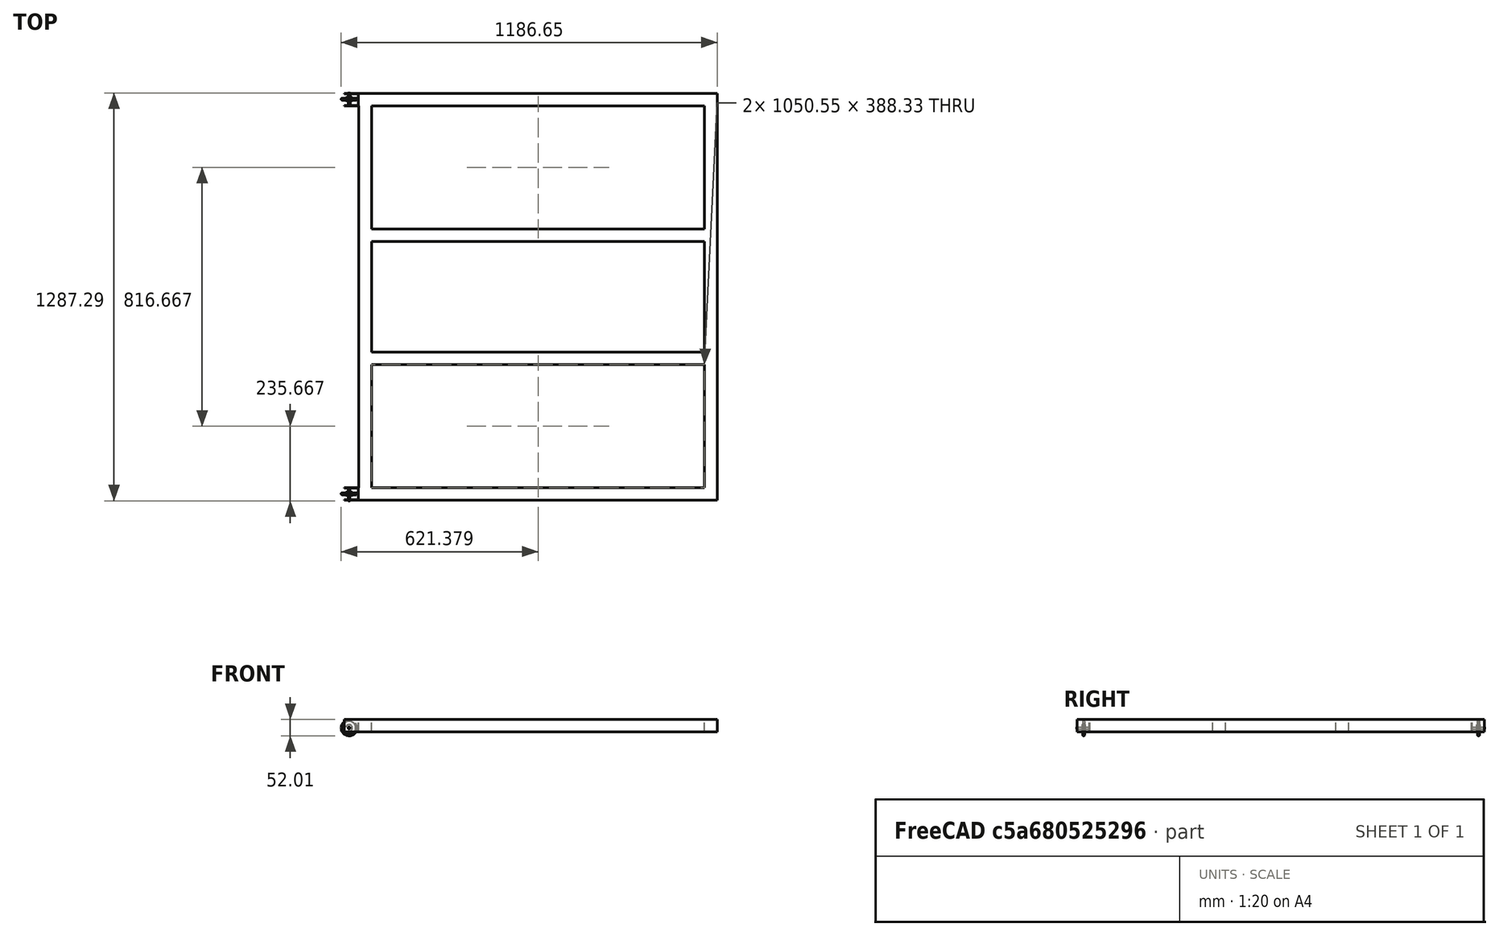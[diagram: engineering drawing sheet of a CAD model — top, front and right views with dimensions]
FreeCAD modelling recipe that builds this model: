
FCSTD DOCUMENT  (FreeCAD 0.19R24267 +148 (Git))
Label: planche jacuzzyV2
License: All rights reserved
LicenseURL: http://en.wikipedia.org/wiki/All_rights_reserved
objects: TechDraw::DrawViewDimension×9, PartDesign::Body×3, TechDraw::DrawViewPart×3, Sketcher::SketchObject×2, TechDraw::DrawViewDetail×2, PartDesign::Pad×1, PartDesign::Mirrored×1, TechDraw::DrawSVGTemplate×1, TechDraw::DrawProjGroupItem×1, TechDraw::DrawProjGroup×1, PartDesign::Revolution×1, PartDesign::FeatureBase×1, TechDraw::DrawViewSymbol×1, TechDraw::DrawPage×1
note: 11 computed .brp shape members not serialized (recipe doc carries the construction recipe); baked Part::Feature solids carry a one-line shape summary decoded from their .brp

FEATURE [Sketcher::SketchObject] Sketch
  FullyConstrained = false
  MapMode = 5
  Support = -> [XY_Plane]
  sketch-geometry (20):
    g0: LineSegment StartX=-403.347 StartY=642.5 StartZ=0 EndX=773.653 EndY=642.5 EndZ=0
    g1: LineSegment StartX=773.653 StartY=642.5 StartZ=0 EndX=733.653 EndY=602.5 EndZ=0
    g2: LineSegment StartX=733.653 StartY=602.5 StartZ=0 EndX=-316.896 EndY=602.5 EndZ=0
    g3: LineSegment StartX=-403.347 StartY=602.5 StartZ=0 EndX=-403.347 EndY=604 EndZ=0
    g4: LineSegment StartX=733.653 StartY=602.5 StartZ=0 EndX=773.653 EndY=642.5 EndZ=0
    g5: LineSegment StartX=773.653 StartY=642.5 StartZ=0 EndX=773.653 EndY=0 EndZ=0
    g6: LineSegment StartX=773.653 StartY=0 StartZ=0 EndX=733.653 EndY=0 EndZ=0
    g7: LineSegment StartX=733.653 StartY=0 StartZ=0 EndX=733.653 EndY=174.167 EndZ=0
    g8: LineSegment StartX=-316.896 StartY=602.5 StartZ=0 EndX=-316.896 EndY=214.167 EndZ=0
    g9: LineSegment StartX=-316.896 StartY=0 StartZ=0 EndX=-356.896 EndY=0 EndZ=0
    g10: LineSegment StartX=-356.896 StartY=0 StartZ=0 EndX=-356.896 EndY=602.5 EndZ=0
    g11: LineSegment StartX=-356.896 StartY=602.5 StartZ=0 EndX=-403.347 EndY=602.5 EndZ=0
    g12: LineSegment StartX=-316.896 StartY=214.167 StartZ=0 EndX=733.653 EndY=214.167 EndZ=0
    g13: LineSegment StartX=733.653 StartY=174.167 StartZ=0 EndX=-316.896 EndY=174.167 EndZ=0
    g14: LineSegment StartX=733.653 StartY=214.167 StartZ=0 EndX=733.653 EndY=602.5 EndZ=0
    g15: LineSegment StartX=-316.896 StartY=174.167 StartZ=0 EndX=-316.896 EndY=0 EndZ=0
    g16: LineSegment StartX=-403.347 StartY=641 StartZ=0 EndX=-358.347 EndY=641 EndZ=0
    g17: LineSegment StartX=-358.347 StartY=641 StartZ=0 EndX=-358.347 EndY=604 EndZ=0
    g18: LineSegment StartX=-358.347 StartY=604 StartZ=0 EndX=-403.347 EndY=604 EndZ=0
    g19: LineSegment StartX=-403.347 StartY=641 StartZ=0 EndX=-403.347 EndY=642.5 EndZ=0
  constraints (52):
    c: Coincident(g0,g1)
    c: Coincident(g1,g2)
    c: Coincident(g11,g3)
    c: Coincident(g19,g0)
    c: Horizontal(g0)
    c: Horizontal(g2)
    c: Vertical(g3)
    c: DistanceY(g3,g19) = 40
    c: DistanceX(g0,g0) = 1177
    c: Angle(g0,g1) = 0.785398
    c: DistanceY(g-1,g0) = 642.5
    c: Coincident(g4,g5)
    c: Coincident(g5,g6)
    c: Coincident(g6,g7)
    c: Coincident(g14,g4)
    c: Horizontal(g6)
    c: Vertical(g5)
    c: Vertical(g7)
    c: PointOnObject(g5,g-1)
    c: Coincident(g4,g1)
    c: Coincident(g0,g4)
    c: Coincident(g15,g9)
    c: Coincident(g9,g10)
    c: Horizontal(g9)
    c: Vertical(g8)
    c: Vertical(g10)
    c: PointOnObject(g15,g-1)
    c: DistanceX(g9,g9) = 40
    c: Tangent(g2,g11)
    c: Horizontal(g12)
    c: Horizontal(g13)
    c: DistanceY(g13,g12) = 40
    c: Tangent(g7,g14)
    c: Coincident(g8,g12)
    c: Tangent(g8,g15)
    c: DistanceY(g12,g1) = 388.333
    c: Coincident(g7,g13)
    c: Coincident(g13,g15)
    c: Coincident(g8,g2)
    c: Coincident(g11,g10)
    c: Coincident(g14,g12)
    c: Horizontal(g16)
    c: Coincident(g16,g17)
    c: Vertical(g17)
    c: Coincident(g17,g18)
    c: Horizontal(g18)
    c: DistanceY(g16,g0) = 1.5
    c: DistanceY(g3,g18) = 1.5
    c: DistanceX(g16,g16) = 45
    c: Coincident(g3,g18)
    c: Coincident(g19,g16)
    c: Tangent(g3,g19)
FEATURE [PartDesign::Pad] Pad
  Direction = (1,1,1)
  Length = 40
  Length2 = 100
  Profile = -> Sketch
  Type = 0
FEATURE [PartDesign::Mirrored] Mirrored
  BaseFeature = -> Pad
  MirrorPlane = -> XZ_Plane
  Originals = -> [Pad]
FEATURE [PartDesign::Body] Body
  Group = -> [Sketch,Pad,Mirrored]
  Origin = -> Origin
  Tip = -> Mirrored
FEATURE [TechDraw::DrawSVGTemplate] Template
  EditableTexts = Designed_by_Name=Labrit Yvan; Drawing_number=Drawing number; FC-Date=20/06/2022; FC-SC=Scale; FC-SH=Sheet; FC-Title=Trappe Jacuzzi; Subtitle=Subtitle; Weight=Weight
  Height = 210
  Orientation = 1
  Width = 297
FEATURE [TechDraw::DrawViewPart] View
  CoarseView = false
  Direction = (-0.472,0.816,0.334)
  Focus = 100
  HardHidden = false
  IsoCount = 0
  IsoHidden = false
  IsoVisible = false
  LockPosition = false
  Perspective = false
  Rotation = 0
  Scale = 0.08
  ScaleType = 0
  SeamHidden = false
  SeamVisible = true
  SmoothHidden = false
  SmoothVisible = true
  Source = -> [Mirrored]
  X = 208.733
  XDirection = (-0.861,-0.508,0.024)
  Y = 152.393
FEATURE [TechDraw::DrawProjGroupItem] ProjItem001  label="Front001"
  CoarseView = false
  Direction = (0,0,1)
  Focus = 100
  HardHidden = false
  IsoCount = 0
  IsoHidden = false
  IsoVisible = false
  LockPosition = true
  Perspective = false
  Rotation = 0
  RotationVector = (0,-1,0)
  Scale = 0.05
  ScaleType = 2
  SeamHidden = false
  SeamVisible = true
  SmoothHidden = false
  SmoothVisible = true
  Source = -> [Mirrored]
  Type = 0
  X = 0
  XDirection = (0,-1,0)
  Y = 0
FEATURE [TechDraw::DrawProjGroup] ProjGroup001
  Anchor = -> ProjItem001
  AutoDistribute = true
  LockPosition = false
  ProjectionType = 0
  Rotation = 0
  Scale = 0.05
  ScaleType = 0
  Source = -> [Mirrored]
  Views = -> [ProjItem001]
  X = 97.9019
  Y = 147.642
  spacingX = 15
  spacingY = 15
FEATURE [TechDraw::DrawViewDimension] Dimension
  Arbitrary = false
  ArbitraryTolerances = false
  EqualTolerance = true
  FormatSpec = %.2f
  FormatSpecOverTolerance = %+.2f
  FormatSpecUnderTolerance = %+.2f
  Inverted = false
  LockPosition = false
  MeasureType = 1
  OverTolerance = 0
  References2D = -> [ProjItem001]
  Rotation = 0
  ScaleType = 0
  TheoreticalExact = false
  Type = 1
  UnderTolerance = 0
  X = 0.655236
  Y = 47.7513
FEATURE [TechDraw::DrawViewDimension] Dimension002
  Arbitrary = false
  ArbitraryTolerances = false
  EqualTolerance = true
  FormatSpec = %.2f
  FormatSpecOverTolerance = %+.2f
  FormatSpecUnderTolerance = %+.2f
  Inverted = false
  LockPosition = false
  MeasureType = 1
  OverTolerance = 0
  References2D = -> [ProjItem001]
  Rotation = 0
  ScaleType = 0
  TheoreticalExact = false
  Type = 2
  UnderTolerance = 0
  X = -51.0961
  Y = -0.556748
FEATURE [TechDraw::DrawViewDimension] Dimension003
  Arbitrary = false
  ArbitraryTolerances = false
  EqualTolerance = true
  FormatSpec = %.2f
  FormatSpecOverTolerance = %+.2f
  FormatSpecUnderTolerance = %+.2f
  Inverted = false
  LockPosition = false
  MeasureType = 1
  OverTolerance = 0
  References2D = -> [ProjItem001]
  Rotation = 0
  ScaleType = 0
  TheoreticalExact = false
  Type = 2
  UnderTolerance = 0
  X = -41.8667
  Y = -0.060316
FEATURE [TechDraw::DrawViewDetail] Detail
  AnchorPoint = (-632.6,-575,0)
  BaseView = -> ProjItem001
  CoarseView = false
  Direction = (0,0,1)
  Focus = 100
  HardHidden = false
  IsoCount = 0
  IsoHidden = false
  IsoVisible = false
  LockPosition = false
  Perspective = false
  Radius = 50
  Reference = 1
  Rotation = 0
  Scale = 0.25
  ScaleType = 2
  SeamHidden = false
  SeamVisible = true
  SmoothHidden = false
  SmoothVisible = true
  Source = -> [Mirrored]
  X = 38.5
  XDirection = (0,-1,0)
  Y = 100
FEATURE [TechDraw::DrawViewDimension] Dimension006
  Arbitrary = false
  ArbitraryTolerances = false
  EqualTolerance = true
  FormatSpec = %.2f
  FormatSpecOverTolerance = %+.2f
  FormatSpecUnderTolerance = %+.2f
  Inverted = false
  LockPosition = false
  MeasureType = 1
  OverTolerance = 0
  References2D = -> [Detail]
  Rotation = 0
  ScaleType = 0
  TheoreticalExact = false
  Type = 1
  UnderTolerance = 0
  X = 10.4892
  Y = -7.04453
FEATURE [TechDraw::DrawViewDimension] Dimension007
  Arbitrary = false
  ArbitraryTolerances = false
  EqualTolerance = true
  FormatSpec = %.2f
  FormatSpecOverTolerance = %+.2f
  FormatSpecUnderTolerance = %+.2f
  Inverted = false
  LockPosition = false
  MeasureType = 1
  OverTolerance = 0
  References2D = -> [Detail]
  Rotation = 0
  ScaleType = 0
  TheoreticalExact = false
  Type = 2
  UnderTolerance = 0
  X = -11.7591
  Y = -11.4692
FEATURE [TechDraw::DrawViewDetail] Detail001  label="Detail 2"
  AnchorPoint = (179.3,-292.9,0)
  BaseView = -> View
  CoarseView = false
  Direction = (-0.472,0.816,0.334)
  Focus = 100
  HardHidden = false
  IsoCount = 0
  IsoHidden = false
  IsoVisible = false
  LockPosition = false
  Perspective = false
  Radius = 50
  Reference = 2
  Rotation = 0
  Scale = 0.25
  ScaleType = 2
  SeamHidden = false
  SeamVisible = true
  SmoothHidden = false
  SmoothVisible = true
  Source = -> [Mirrored]
  X = 258.5
  XDirection = (-0.861,-0.508,0.024)
  Y = 115
FEATURE [TechDraw::DrawViewDimension] Dimension001
  Arbitrary = false
  ArbitraryTolerances = false
  EqualTolerance = true
  FormatSpec = %.2f
  FormatSpecOverTolerance = %+.2f
  FormatSpecUnderTolerance = %+.2f
  Inverted = false
  LockPosition = false
  MeasureType = 1
  OverTolerance = 0
  References2D = -> [ProjItem001]
  Rotation = 0
  ScaleType = 0
  TheoreticalExact = false
  Type = 1
  UnderTolerance = 0
  X = -0.214143
  Y = 42.4702
FEATURE [TechDraw::DrawViewDimension] Dimension008
  Arbitrary = false
  ArbitraryTolerances = false
  EqualTolerance = true
  FormatSpec = %.2f
  FormatSpecOverTolerance = %+.2f
  FormatSpecUnderTolerance = %+.2f
  Inverted = false
  LockPosition = false
  MeasureType = 1
  OverTolerance = 0
  References2D = -> [ProjItem001]
  Rotation = 0
  ScaleType = 0
  TheoreticalExact = false
  Type = 1
  UnderTolerance = 0
  X = -21.4956
  Y = 35.7089
FEATURE [TechDraw::DrawViewDimension] Dimension009
  Arbitrary = false
  ArbitraryTolerances = false
  EqualTolerance = true
  FormatSpec = %.2f
  FormatSpecOverTolerance = %+.2f
  FormatSpecUnderTolerance = %+.2f
  Inverted = false
  LockPosition = false
  MeasureType = 1
  OverTolerance = 0
  References2D = -> [ProjItem001]
  Rotation = 0
  ScaleType = 0
  TheoreticalExact = false
  Type = 1
  UnderTolerance = 0
  X = -0.877062
  Y = 36.0378
FEATURE [TechDraw::DrawViewDimension] Dimension010
  Arbitrary = false
  ArbitraryTolerances = false
  EqualTolerance = true
  FormatSpec = %.2f
  FormatSpecOverTolerance = %+.2f
  FormatSpecUnderTolerance = %+.2f
  Inverted = false
  LockPosition = false
  MeasureType = 1
  OverTolerance = 0
  References2D = -> [ProjItem001]
  Rotation = 0
  ScaleType = 0
  TheoreticalExact = false
  Type = 1
  UnderTolerance = 0
  X = 21.1667
  Y = 35.7089
FEATURE [Sketcher::SketchObject] Sketch002  label="Roue"
  FullyConstrained = false
  MapMode = 5
  Placement = pos=(0,0,0) rot=(0.57735,0.57735,0.57735;2.0944rad)
  Support = -> [YZ_Plane001]
  sketch-geometry (14):
    g0: LineSegment StartX=4.93451 StartY=3.125 StartZ=0 EndX=4.93451 EndY=10.2612 EndZ=0
    g1: LineSegment StartX=4.93451 StartY=10.2612 StartZ=0 EndX=3.21857 EndY=10.2612 EndZ=0
    g2: LineSegment StartX=3.21857 StartY=10.2612 StartZ=0 EndX=3.21857 EndY=20.8771 EndZ=0
    g3: LineSegment StartX=-3.21857 StartY=20.8771 StartZ=0 EndX=-3.21857 EndY=10.2612 EndZ=0
    g4: LineSegment StartX=-3.21857 StartY=10.2612 StartZ=0 EndX=-4.93451 EndY=10.2612 EndZ=0
    g5: LineSegment StartX=-4.93451 StartY=10.2612 StartZ=0 EndX=-4.93451 EndY=3.125 EndZ=0
    g6: LineSegment StartX=-15.8189 StartY=0 StartZ=0 EndX=22.6988 EndY=0 EndZ=0
    g7: ArcOfCircle CenterX=0 CenterY=21.6822 CenterZ=0 NormalX=0 NormalY=0 NormalZ=1 AngleXU=0 Radius=3.31775 StartAngle=6.03805 EndAngle=9.66992
    g8: LineSegment StartX=-4.99153 StartY=25 StartZ=0 EndX=4.87713 EndY=25 EndZ=0
    g9: LineSegment StartX=-21.9976 StartY=3.125 StartZ=0 EndX=-4.93451 EndY=3.125 EndZ=0
    g10: LineSegment StartX=19.2851 StartY=3.125 StartZ=0 EndX=19.2851 EndY=0 EndZ=0
    g11: LineSegment StartX=19.2851 StartY=0 StartZ=0 EndX=-21.9976 EndY=0 EndZ=0
    g12: LineSegment StartX=-21.9976 StartY=0 StartZ=0 EndX=-21.9976 EndY=3.125 EndZ=0
    g13: LineSegment StartX=4.93451 StartY=3.125 StartZ=0 EndX=19.2851 EndY=3.125 EndZ=0
  constraints (32):
    c: Vertical(g0)
    c: Coincident(g0,g1)
    c: Horizontal(g1)
    c: Coincident(g1,g2)
    c: Vertical(g2)
    c: Vertical(g3)
    c: Coincident(g3,g4)
    c: Horizontal(g4)
    c: Coincident(g4,g5)
    c: Vertical(g5)
    c: PointOnObject(g6,g-1)
    c: PointOnObject(g6,g-1)
    c: DistanceY(g-1,g0) = 3.125
    c: Coincident(g7,g3)
    c: Coincident(g7,g2)
    c: Horizontal(g8)
    c: Tangent(g8,g7)
    c: DistanceY(g-1,g8) = 25
    c: PointOnObject(g7,g-2)
    c: Symmetric(g3,g1,g-2)
    c: Coincident(g13,g10)
    c: Coincident(g10,g11)
    c: Coincident(g11,g12)
    c: Coincident(g12,g9)
    c: Horizontal(g9)
    c: Horizontal(g11)
    c: Vertical(g10)
    c: Vertical(g12)
    c: PointOnObject(g10,g6)
    c: Coincident(g9,g5)
    c: Coincident(g13,g0)
    c: Tangent(g9,g13)
FEATURE [PartDesign::Revolution] Revolution
  Angle = 360
  Axis = (1.28e-14,38.5177,-8.6e-15)
  Base = (-5.3e-15,-15.8189,3.5e-15)
  Placement = pos=(0,0,0) rot=(0.57735,0.57735,0.57735;2.0944rad)
  Profile = -> Sketch002
  ReferenceAxis = -> Sketch002 [Axis0]
FEATURE [PartDesign::Body] Body001  label="body roue"
  Group = -> [Sketch002,Revolution]
  Origin = -> Origin001
  Placement = pos=(-387.855,624,12.9911) rot=(0,-1,0;1.0472rad)
  Tip = -> Revolution
FEATURE [PartDesign::FeatureBase] Clone
  BaseFeature = -> Revolution
  Placement = pos=(0,0,0) rot=(0.57735,0.57735,0.57735;2.0944rad)
FEATURE [PartDesign::Body] Body002
  BaseFeature = -> Revolution
  Group = -> [Clone]
  Origin = -> Origin002
  Placement = pos=(-388,-622,13) rot=(0,0,1;0rad)
  Tip = -> Clone
FEATURE [TechDraw::DrawViewPart] View001
  CoarseView = false
  Direction = (0,0,-1)
  Focus = 100
  HardHidden = false
  IsoCount = 0
  IsoHidden = false
  IsoVisible = false
  LockPosition = false
  Perspective = false
  Rotation = 0
  Scale = 0.05
  ScaleType = 0
  SeamHidden = false
  SeamVisible = true
  SmoothHidden = false
  SmoothVisible = true
  Source = -> [Body001,Body002]
  X = 98.368
  XDirection = (0,1,0)
  Y = 118.9
FEATURE [TechDraw::DrawViewSymbol] ActiveView
  LockPosition = false
  Rotation = 0
  ScaleType = 2
  X = 148.5
  Y = 105
FEATURE [TechDraw::DrawViewPart] View002
  CoarseView = false
  Direction = (-0.707,0.5,0.5)
  Focus = 100
  HardHidden = false
  IsoCount = 0
  IsoHidden = false
  IsoVisible = false
  LockPosition = false
  Perspective = false
  Rotation = 0
  ScaleType = 0
  SeamHidden = false
  SeamVisible = true
  SmoothHidden = false
  SmoothVisible = true
  Source = -> [Origin]
  X = 148.5
  XDirection = (-0.5,-0.854,0.146)
  Y = 105
FEATURE [TechDraw::DrawPage] Page
  KeepUpdated = true
  NextBalloonIndex = 1
  ProjectionType = 0
  Template = -> Template
  Views = -> [View,ProjGroup001,Dimension,Dimension001,Dimension002,Dimension003,Detail,Dimension006,Dimension007,Detail001,Dimension008,Dimension009,Dimension010,View001,ActiveView,View002]
